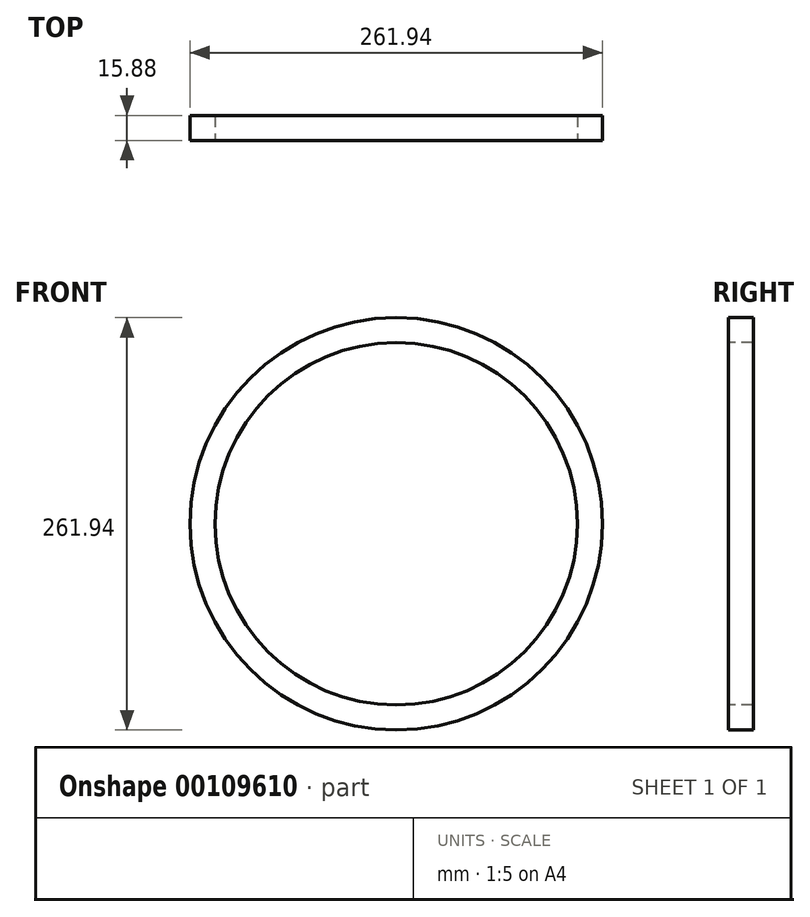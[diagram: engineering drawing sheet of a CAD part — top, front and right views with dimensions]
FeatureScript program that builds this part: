
annotation { "Feature Type Name" : "Feature", "Feature Type Description" : "" }
export const myFeature = defineFeature(function(context is Context, id is Id, definition is map)
    precondition{}
    {
        {
            var Q0;
            Q0=qCreatedBy(makeId("Front.planeOp"),FACE);
            var sketch = newSketch(context, id + "F0", { "sketchPlane" : qUnion([Q0])});
            skCircle(sketch, "E0", {"center": v(0, 0) * mm, "radius": 115.1 * mm});
            skCircle(sketch, "E1", {"center": v(0, 0) * mm, "radius": 130.97 * mm});
            skSolve(sketch);
        }
        {
            var Q0;
            Q0=sQuery(id+"F0.wireOp",EDGE,"E1");
            var Q1;
            Q1=sQuery(id+"F0.wireOp",EDGE,"E0");
            extrude(context, id + "F1", {"bodyType" : ToolBodyType.SURFACE, "surfaceEntities" : qUnion([Q0, Q1]), "depth" : 15.88 * mm});
        }
    });
